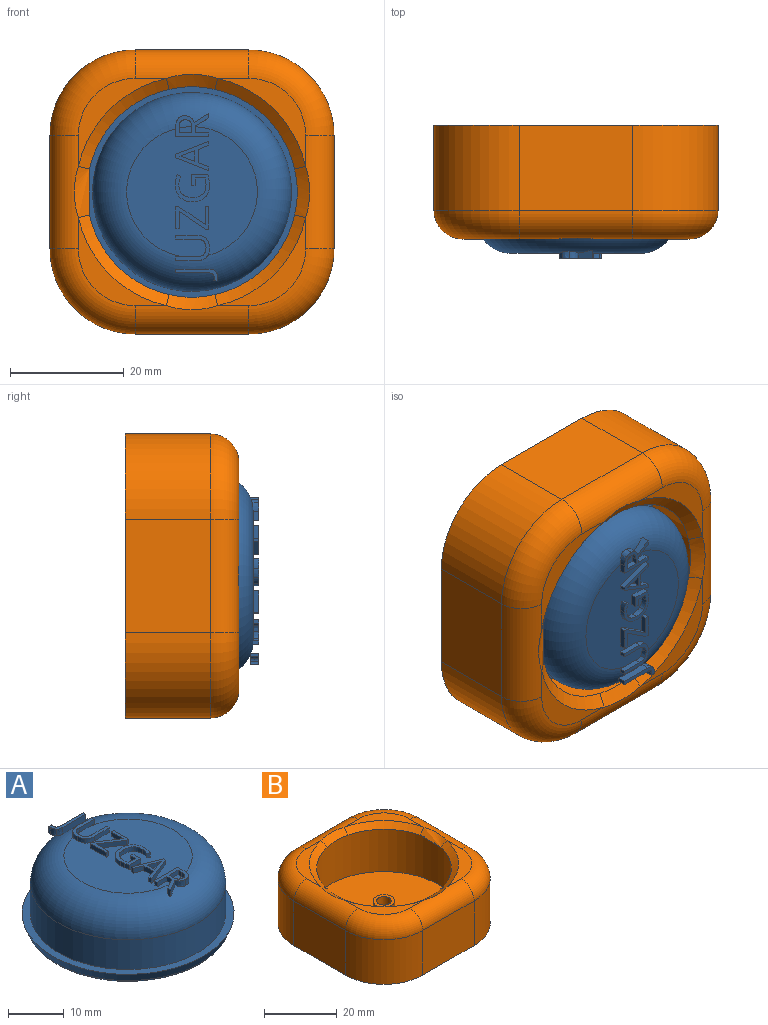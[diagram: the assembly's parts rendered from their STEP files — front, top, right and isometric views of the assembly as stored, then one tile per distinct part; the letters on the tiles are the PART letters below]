
ASSEMBLY  parts=2 mates=1
PART A: 107 faces, bbox 39.7x39.7x21 mm
  f0: plane 23x22.88mm, normal (0,0,1), area 372.6mm2, adj f6,f23,f24,f25,f26,f27,f28,f29
  f1: cylinder r=17.5mm len=35mm, axis (0,0,-1), area 714.7mm2, adj f2,f6
  f2: plane 38x38mm, normal (0,0,1), area 172mm2, adj f1,f4
  f3: plane 34.65x34.65mm, normal (0,0,-1), area 87.4mm2, adj f5,f8
  f4: cone r=19mm half-angle=21.8deg, axis (0,0,1), area 235.9mm2, adj f2,f5
  f5: torus R=17.32mm, axis (0,0,1), area 133.5mm2, adj f3,f4
  f6: torus R=11.5mm, axis (0,0,1), area 894.9mm2, adj f0,f1,f13,f14,f15,f22,f30,f31
  f7: cylinder r=1.75mm len=12mm, axis (0,0,-1), area 131.9mm2, adj f9,f10
  f8: cylinder r=16.5mm len=33mm, axis (0,0,-1), area 725.7mm2, adj f3,f9
  f9: plane 33x33mm, normal (0,0,-1), area 845.7mm2, adj f7,f8
  f10: plane 3.5x3.5mm, normal (0,0,-1), area 9.6mm2, adj f7
  f11: extruded ~1.5x0.59mm, area 0.9mm2, adj f12,f20,f21,f22
  f12: extruded ~1.5x1.1mm, area 1.8mm2, adj f11,f13,f21,f22
  f13: extruded ~1.5x1.18mm, area 1.9mm2, adj f6,f12,f14,f21,f22
  f14: plane 5.78x1.49mm, normal (0,-1,0), area 8.1mm2, adj f6,f13,f15,f21
  f15: plane 1.5x0.68mm, normal (1,0,0), area 1mm2, adj f6,f14,f16,f21,f22
  f16: plane 5.83x1.5mm, normal (0,1,0), area 8.8mm2, adj f15,f17,f21,f22
  f17: extruded ~1.5x0.69mm, area 1.1mm2, adj f16,f18,f21,f22
  f18: extruded ~1.5x0.6mm, area 1mm2, adj f17,f19,f21,f22
  f19: extruded ~1.5x0.59mm, area 0.9mm2, adj f18,f20,f21,f22
  f20: plane 1.5x0.58mm, normal (0,1,0), area 0.9mm2, adj f11,f19,f21,f22
  f21: plane 7.37x2.08mm, normal (0,0,1), area 5.6mm2, adj f11,f12,f13,f14,f15,f16,f17,f18
  f22: plane 7.37x2.08mm, normal (0,0,-1), area 4.2mm2, adj f6,f11,f12,f13,f15,f16,f17,f18
  f23: plane 3.78x1mm, normal (0,-1,0), area 3.8mm2, adj f0,f24,f36,f37
  f24: plane 1x0.68mm, normal (1,0,0), area 0.7mm2, adj f0,f23,f25,f37
  f25: plane 3.8x1mm, normal (0,1,0), area 3.8mm2, adj f0,f24,f26,f37
  f26: extruded ~1.13x1mm, area 1.2mm2, adj f0,f25,f27,f37
  f27: extruded ~1.14x1mm, area 1.2mm2, adj f0,f26,f28,f37
  f28: extruded ~1.17x1mm, area 1.3mm2, adj f0,f27,f29,f37
  f29: extruded ~1.12x1mm, area 1.2mm2, adj f0,f28,f30,f37
  f30: plane 3.85x1.04mm, normal (0,-1,0), area 3.8mm2, adj f0,f6,f29,f31,f37
  f31: plane 1.07x0.69mm, normal (1,0,0), area 0.7mm2, adj f6,f30,f32,f37
  f32: plane 3.76x1.07mm, normal (0,1,0), area 3.9mm2, adj f6,f31,f33,f37
  f33: extruded ~1.58x1.03mm, area 1.8mm2, adj f6,f32,f34,f37
  f34: extruded ~1.63x1.01mm, area 1.8mm2, adj f0,f6,f33,f35,f37
  f35: extruded ~1.66x1mm, area 1.8mm2, adj f0,f34,f36,f37
  f36: extruded ~1.57x1mm, area 1.7mm2, adj f0,f23,f35,f37
  f37: plane 5.92x4.47mm, normal (0,0,1), area 9mm2, adj f23,f24,f25,f26,f27,f28,f29,f30
  f38: plane 4.01x1mm, normal (-1,0,0), area 4mm2, adj f0,f39,f47,f48
  f39: plane 1x0.61mm, normal (0,-1,0), area 0.6mm2, adj f0,f38,f40,f48
  f40: plane 3.19x1mm, normal (1,0,0), area 3.2mm2, adj f0,f39,f41,f48
  f41: plane 4.69x3.1mm, normal (-0.55,-0.83,0), area 5.6mm2, adj f0,f40,f42,f48
  f42: plane 1x0.53mm, normal (0,-1,0), area 0.5mm2, adj f0,f41,f43,f48
  f43: plane 3.83x1mm, normal (1,0,0), area 3.8mm2, adj f0,f42,f44,f48
  f44: plane 1x0.61mm, normal (0,1,0), area 0.6mm2, adj f0,f43,f45,f48
  f45: plane 3x1mm, normal (-1,0,0), area 3mm2, adj f0,f44,f46,f48
  f46: plane 4.69x3.1mm, normal (0.55,0.83,0), area 5.6mm2, adj f0,f45,f47,f48
  f47: plane 1x0.53mm, normal (0,1,0), area 0.5mm2, adj f0,f38,f46,f48
  f48: plane 5.83x4.01mm, normal (0,0,1), area 8.4mm2, adj f38,f39,f40,f41,f42,f43,f44,f45
  f49: plane 1.98x1mm, normal (1,0,0), area 2mm2, adj f0,f50,f68,f69
  f50: plane 1x0.61mm, normal (0,1,0), area 0.6mm2, adj f0,f49,f51,f69
  f51: plane 1.3x1mm, normal (-1,0,0), area 1.3mm2, adj f0,f50,f52,f69
  f52: plane 1.8x1mm, normal (0,1,0), area 1.8mm2, adj f0,f51,f53,f69
  f53: extruded ~1.19x1mm, area 1.2mm2, adj f0,f52,f54,f69
  f54: extruded ~1.69x1mm, area 1.9mm2, adj f0,f53,f55,f69
  f55: extruded ~1.79x1mm, area 1.9mm2, adj f0,f54,f56,f69
  f56: extruded ~1.76x1mm, area 1.9mm2, adj f0,f55,f57,f69
  f57: extruded ~1.66x1mm, area 1.8mm2, adj f0,f56,f58,f69
  f58: extruded ~1.52x1mm, area 1.6mm2, adj f0,f57,f59,f69
  f59: plane 1x0.6mm, normal (-0.4,-0.92,0), area 0.7mm2, adj f0,f58,f60,f69
  f60: extruded ~1.74x1mm, area 1.8mm2, adj f0,f59,f61,f69
  f61: extruded ~1.61x1mm, area 1.7mm2, adj f0,f60,f62,f69
  f62: extruded ~1.05x1.05mm, area 1.5mm2, adj f0,f61,f63,f69
  f63: extruded ~1.6x1mm, area 1.7mm2, adj f0,f62,f64,f69
  f64: extruded ~2.21x1mm, area 2.4mm2, adj f0,f63,f65,f69
  f65: extruded ~2.06x1mm, area 2.3mm2, adj f0,f64,f66,f69
  f66: extruded ~1.11x1mm, area 1.1mm2, adj f0,f65,f67,f69
  f67: extruded ~1x0.94mm, area 1mm2, adj f0,f66,f68,f69
  f68: plane 2.84x1mm, normal (0,-1,0), area 2.8mm2, adj f0,f49,f67,f69
  f69: plane 6x4.85mm, normal (0,0,1), area 10.3mm2, adj f49,f50,f51,f52,f53,f54,f55,f56
  f70: plane 1.81x1mm, normal (-0.35,0.94,0), area 1.9mm2, adj f71,f82,f83,f84
  f71: plane 1.89x1mm, normal (1,0,0), area 1.9mm2, adj f70,f72,f83,f84
  f72: plane 1.81x1mm, normal (-0.35,-0.94,0), area 1.9mm2, adj f71,f73,f83,f84
  f73: extruded ~1x0.84mm, area 0.9mm2, adj f72,f82,f83,f84
  f74: plane 1.86x1mm, normal (-0.36,0.93,0), area 2mm2, adj f0,f75,f81,f83
  f75: plane 1x0.7mm, normal (-1,0,0), area 0.7mm2, adj f0,f74,f76,f83
  f76: plane 5.86x2.3mm, normal (0.36,-0.93,0), area 6.3mm2, adj f0,f75,f77,f83
  f77: plane 1x0.57mm, normal (1,0,0), area 0.6mm2, adj f0,f76,f78,f83
  f78: plane 5.86x2.31mm, normal (0.37,0.93,0), area 6.3mm2, adj f0,f77,f79,f83
  f79: plane 1x0.69mm, normal (-1,0,0), area 0.7mm2, adj f0,f78,f80,f83
  f80: plane 1.86x1mm, normal (-0.36,-0.93,0), area 2mm2, adj f0,f79,f81,f83
  f81: plane 2.34x1mm, normal (-1,0,0), area 2.3mm2, adj f0,f74,f80,f83
  f82: extruded ~1x0.84mm, area 0.9mm2, adj f70,f73,f83,f84
  f83: plane 5.86x5.17mm, normal (0,0,1), area 8.8mm2, adj f70,f71,f72,f73,f74,f75,f76,f77
  f84: plane 2.65x1.89mm, normal (0,0,1), area 2.4mm2, adj f70,f71,f72,f73,f82
  f85: plane 1x0.93mm, normal (1,0,0), area 0.9mm2, adj f86,f102,f103,f106
  f86: plane 2.23x1mm, normal (0,-1,0), area 2.2mm2, adj f85,f87,f103,f106
  f87: plane 1x0.88mm, normal (-1,0,0), area 0.9mm2, adj f86,f88,f103,f105,f106
  f88: extruded ~1.1x1.09mm, area 1.2mm2, adj f87,f89,f103,f105
  f89: extruded ~1.14x0.83mm, area 1mm2, adj f88,f90,f103,f105
  f90: extruded ~1.14x0.86mm, area 1mm2, adj f89,f102,f103,f105
  f91: plane 2.43x1mm, normal (0,-1,0), area 2.4mm2, adj f0,f92,f101,f103
  f92: plane 1.22x1mm, normal (-1,0,0), area 1.2mm2, adj f0,f6,f91,f93,f103
  f93: plane 2.43x1.41mm, normal (-0.5,0.86,0), area 3.1mm2, adj f6,f92,f94,f103
  f94: plane 1.5x0.81mm, normal (-1,0,0), area 1.1mm2, adj f6,f93,f95,f103,f104
  f95: plane 2.62x1.59mm, normal (0.52,-0.86,0), area 3.9mm2, adj f6,f94,f96,f103,f104
  f96: extruded ~1.56x1.33mm, area 2.5mm2, adj f6,f95,f97,f103
  f97: extruded ~1.33x1.24mm, area 1.8mm2, adj f6,f96,f98,f103
  f98: extruded ~1.59x1.23mm, area 1.8mm2, adj f6,f97,f99,f103
  f99: plane 1.6x1mm, normal (1,0,0), area 1.6mm2, adj f0,f6,f98,f100,f103
  f100: plane 5.83x1mm, normal (0,1,0), area 5.8mm2, adj f0,f99,f101,f103
  f101: plane 1x0.68mm, normal (-1,0,0), area 0.7mm2, adj f0,f91,f100,f103
  f102: extruded ~1.07x1.05mm, area 1.1mm2, adj f85,f90,f103,f105,f106
  f103: plane 5.83x4.11mm, normal (0,0,1), area 10.2mm2, adj f85,f86,f87,f88,f89,f90,f91,f92
  f104: plane 0.32x0.26mm, normal (0,0,-1), area 0mm2, adj f6,f94,f95
  f105: torus R=11.5mm, axis (0,0,1), area 2.4mm2, adj f87,f88,f89,f90,f102,f106
  f106: plane 2.23x1.1mm, normal (0,0,1), area 2.3mm2, adj f85,f86,f87,f102,f105
PART B: 40 faces, bbox 52.6x52.6x20.1 mm
  f0: plane 15.5x15.5mm, normal (0,0,1), area 51.5mm2, adj f26,f28,f30,f37
  f1: plane 15.5x15.5mm, normal (0,0,1), area 51.5mm2, adj f29,f30,f31,f33
  f2: plane 15.5x15.5mm, normal (0,0,1), area 51.5mm2, adj f25,f27,f29,f34
  f3: cylinder r=18.5mm len=13.99mm, axis (0,0,1), area 0mm2, adj f13,f38
  f4: cylinder r=18.5mm len=13.99mm, axis (0,0,1), area 0mm2, adj f13,f34
  f5: cylinder r=18.5mm len=13.99mm, axis (0,0,1), area 0mm2, adj f13,f33
  f6: plane 20x15mm, normal (0,1,0), area 300mm2, adj f11,f20,f23,f29
  f7: plane 20x15mm, normal (-1,0,0), area 300mm2, adj f11,f20,f21,f30
  f8: plane 20x15mm, normal (0,-1,0), area 300mm2, adj f11,f21,f22,f26
  f9: plane 20x15mm, normal (1,0,0), area 300mm2, adj f11,f22,f23,f25
  f10: plane 15.5x15.5mm, normal (0,0,1), area 51.5mm2, adj f24,f25,f26,f38
  f11: plane 50x50mm, normal (0,0,-1), area 2306.9mm2, adj f6,f7,f8,f9,f20,f21,f22,f23
  f12: cylinder r=18.5mm len=13.99mm, axis (0,0,1), area 0mm2, adj f13,f37
  f13: plane 42.12x42.12mm, normal (0,0,-1), area 309.7mm2, adj f3,f4,f5,f12,f14,f32,f35,f36
  f14: cylinder r=21mm len=42mm, axis (0,0,1), area 2111.2mm2, adj f13,f15
  f15: plane 42x42mm, normal (0,0,1), area 1357.2mm2, adj f14,f17
  f16: cylinder r=2mm len=5mm, axis (0,0,-1), area 62.8mm2, adj f18,f19
  f17: cylinder r=3mm len=6mm, axis (0,0,-1), area 94.2mm2, adj f15,f18
  f18: plane 6x6mm, normal (0,0,1), area 15.7mm2, adj f16,f17
  f19: plane 4x4mm, normal (0,0,1), area 12.6mm2, adj f16
  f20: cylinder r=15mm len=15mm, axis (0,0,1), area 353.4mm2, adj f6,f7,f11,f31
  f21: cylinder r=15mm len=15mm, axis (0,0,-1), area 353.4mm2, adj f7,f8,f11,f28
  f22: cylinder r=15mm len=15mm, axis (0,0,1), area 353.4mm2, adj f8,f9,f11,f24
  f23: cylinder r=15mm len=15mm, axis (0,0,-1), area 353.4mm2, adj f6,f9,f11,f27
  f24: torus R=10mm, axis (0,0,1), area 162.6mm2, adj f10,f22,f25,f26
  f25: cylinder r=5mm len=20mm, axis (0,-1,0), area 152.8mm2, adj f2,f9,f10,f24,f27,f36
  f26: cylinder r=5mm len=20mm, axis (-1,0,0), area 152.8mm2, adj f0,f8,f10,f24,f28,f39
  f27: torus R=10mm, axis (0,0,1), area 162.6mm2, adj f2,f23,f25,f29
  f28: torus R=10mm, axis (0,0,1), area 162.6mm2, adj f0,f21,f26,f30
  f29: cylinder r=5mm len=20mm, axis (1,0,0), area 152.8mm2, adj f1,f2,f6,f27,f31,f32
  f30: cylinder r=5mm len=20mm, axis (0,1,0), area 152.8mm2, adj f0,f1,f7,f28,f31,f35
  f31: torus R=10mm, axis (0,0,1), area 162.6mm2, adj f1,f20,f29,f30
  f32: bspline ~9x2.67mm, area 22.6mm2, adj f13,f29,f33,f34
  f33: cone r=18.5mm half-angle=53.3deg, axis (0,0,1), area 54.9mm2, adj f1,f5,f32,f35
  f34: cone r=18.5mm half-angle=53.3deg, axis (0,0,1), area 54.9mm2, adj f2,f4,f32,f36
  f35: bspline ~9x2.67mm, area 22.6mm2, adj f13,f30,f33,f37
  f36: bspline ~9x2.67mm, area 22.6mm2, adj f13,f25,f34,f38
  f37: cone r=18.5mm half-angle=53.3deg, axis (0,0,1), area 54.9mm2, adj f0,f12,f35,f39
  f38: cone r=18.5mm half-angle=53.3deg, axis (0,0,1), area 54.9mm2, adj f3,f10,f36,f39
  f39: bspline ~9x2.67mm, area 22.6mm2, adj f13,f26,f37,f38
PLACE A rot(axis=(0,-0.71,0.71),180deg) t=(0,-7.5,0)mm
PLACE B rot(axis=(0,-0.71,0.71),180deg) t=(0,0,0)mm
MATE slider A.f8 <-> B.f14  axis (0,1,0) through (0,-14.5,0)mm
